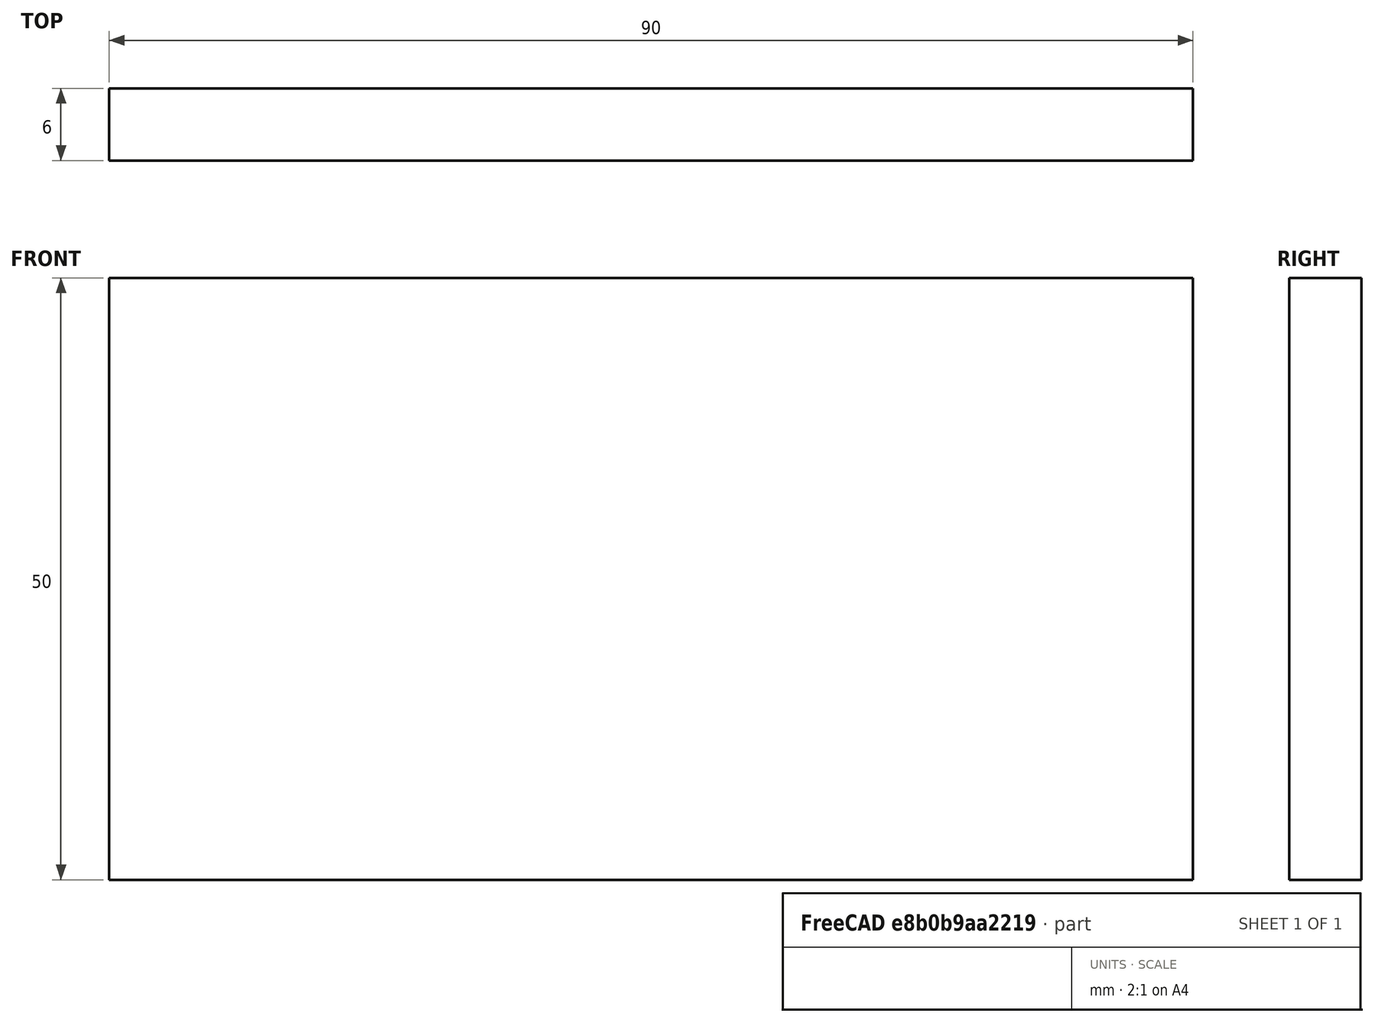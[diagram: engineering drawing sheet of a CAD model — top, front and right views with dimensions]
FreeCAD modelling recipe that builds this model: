
FCSTD DOCUMENT  (FreeCAD 0.15R4671 (Git))
Label: Flat Bar 90x6 EN10058 S235JR
License: All rights reserved
LicenseURL: http://en.wikipedia.org/wiki/All_rights_reserved
objects: Sketcher::SketchObject×1, Part::Extrusion×1
note: 2 computed .brp shape members not serialized (recipe doc carries the construction recipe); baked Part::Feature solids carry a one-line shape summary decoded from their .brp

FEATURE [Sketcher::SketchObject] Sketch
  sketch-geometry (4):
    g0: LineSegment StartX=-45 StartY=-3 StartZ=0 EndX=45 EndY=-3 EndZ=0
    g1: LineSegment StartX=45 StartY=-3 StartZ=0 EndX=45 EndY=3 EndZ=0
    g2: LineSegment StartX=45 StartY=3 StartZ=0 EndX=-45 EndY=3 EndZ=0
    g3: LineSegment StartX=-45 StartY=3 StartZ=0 EndX=-45 EndY=-3 EndZ=0
  constraints (12):
    c: Coincident(g0,g1)
    c: Coincident(g1,g2)
    c: Coincident(g2,g3)
    c: Coincident(g3,g0)
    c: Horizontal(g0)
    c: Horizontal(g2)
    c: Vertical(g1)
    c: Vertical(g3)
    c: Symmetric(g1,g2,g-2)
    c: Symmetric(g0,g1,g-1)
    c: DistanceY(g1) = 6
    c: DistanceX(g0) = 90
FEATURE [Part::Extrusion] Extrude  label="Flat Bar 90x6 EN10058 S235JR"
  Base = -> Sketch
  Dir = (0,0,50)
  Solid = true
